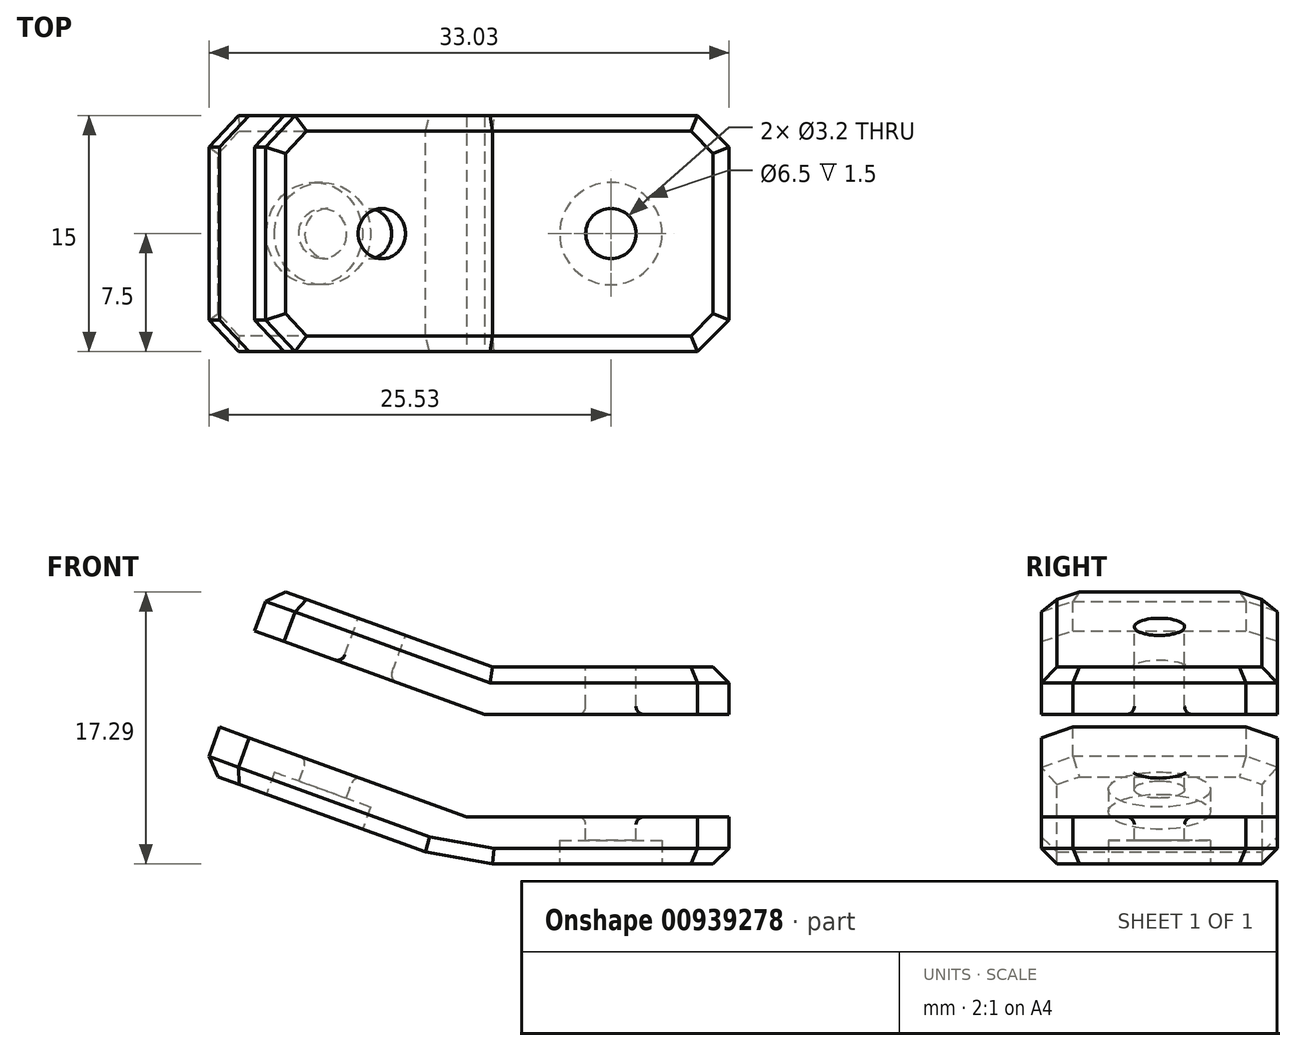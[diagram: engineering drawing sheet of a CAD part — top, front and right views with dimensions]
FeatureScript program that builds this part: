
annotation { "Feature Type Name" : "Feature", "Feature Type Description" : "" }
export const myFeature = defineFeature(function(context is Context, id is Id, definition is map)
    precondition{}
    {
        {
            var Q0;
            Q0=qCreatedBy(makeId("Front.planeOp"),FACE);
            var sketch = newSketch(context, id + "F0", { "sketchPlane" : qUnion([Q0])});
            skLineSegment(sketch, "E0", {"start": v(0, 0) * mm, "end": v(15, 0) * mm});
            skLineSegment(sketch, "E1", {"start": v(0, 0) * mm, "end": v(-14.1, 5.13) * mm});
            skLineSegment(sketch, "E2", {"start": v(-14.1, 5.13) * mm, "end": v(-15.12, 2.31) * mm});
            skLineSegment(sketch, "E3", {"start": v(-15.12, 2.31) * mm, "end": v(-1.03, -2.82) * mm});
            skLineSegment(sketch, "E4", {"start": v(-1.03, -2.82) * mm, "end": v(0, 0) * mm});
            skLineSegment(sketch, "E5", {"start": v(15, 0) * mm, "end": v(15, -3) * mm});
            skLineSegment(sketch, "E6", {"start": v(15, -3) * mm, "end": v(0, -3) * mm});
            skLineSegment(sketch, "E7", {"start": v(0, -3) * mm, "end": v(0, 0) * mm});
            skLineSegment(sketch, "E8", {"start": v(-15.12, 2.31) * mm, "end": v(-17.34, -3.8) * mm, "construction": true});
            skLineSegment(sketch, "E9", {"start": v(-17.34, -3.8) * mm, "end": v(-3.25, -8.93) * mm});
            skLineSegment(sketch, "E10", {"start": v(-3.25, -8.93) * mm, "end": v(-4.28, -11.75) * mm});
            skLineSegment(sketch, "E11", {"start": v(-4.28, -11.75) * mm, "end": v(-18.37, -6.62) * mm});
            skLineSegment(sketch, "E12", {"start": v(-18.37, -6.62) * mm, "end": v(-17.34, -3.8) * mm});
            skLineSegment(sketch, "E13", {"start": v(15, -3) * mm, "end": v(15, -9.5) * mm, "construction": true});
            skLineSegment(sketch, "E14", {"start": v(15, -9.5) * mm, "end": v(0, -9.5) * mm});
            skLineSegment(sketch, "E15", {"start": v(0, -9.5) * mm, "end": v(0, -12.5) * mm});
            skLineSegment(sketch, "E16", {"start": v(0, -12.5) * mm, "end": v(15, -12.5) * mm});
            skLineSegment(sketch, "E17", {"start": v(15, -12.5) * mm, "end": v(15, -9.5) * mm});
            skLineSegment(sketch, "E18", {"start": v(-4.28, -11.75) * mm, "end": v(0, -12.5) * mm});
            skLineSegment(sketch, "E19", {"start": v(-3.25, -8.93) * mm, "end": v(-1.03, -2.82) * mm});
            skLineSegment(sketch, "E20", {"start": v(0, -3) * mm, "end": v(0, -9.5) * mm});
            skSolve(sketch);
        }
        {
            var Q0;
            Q0 = qSketchRegion(id + "F0", true);
            extrude(context, id + "F1", {"entities" : qUnion([Q0]), "depth" : 15 * mm, "offsetDistance" : 25 * mm});
        }
        {
            var Q0;
            Q0=makeQuery(id+"F1.opExtrude","SWEPT_FACE",FACE,{"disambiguationData":[OSD([sQuery(id+"F0.wireOp",EDGE,"E1")])]});
            var sketch = newSketch(context, id + "F2", { "sketchPlane" : qUnion([Q0])});
            skLineSegment(sketch, "E21", {"start": v(-15, -7.5) * mm, "end": v(-7.5, -7.5) * mm, "construction": true});
            skPoint(sketch, "E21.endSnap0", {"position": v(-7.5, -15) * mm});
            skCircle(sketch, "E22", {"center": v(-7.5, -7.5) * mm, "radius": 1.6 * mm});
            skSolve(sketch);
        }
        {
            var Q0;
            Q0 = qSketchRegion(id + "F2", true);
            extrude(context, id + "F3", {"entities" : qUnion([Q0]), "operationType" : NewBodyOperationType.REMOVE, "oppositeDirection" : true, "depth" : 25 * mm, "offsetDistance" : 25 * mm});
        }
        {
            var Q0;
            Q0=makeQuery(id+"F1.opExtrude","SWEPT_FACE",FACE,{"disambiguationData":[OSD([sQuery(id+"F0.wireOp",EDGE,"E0")])]});
            var sketch = newSketch(context, id + "F4", { "sketchPlane" : qUnion([Q0])});
            skLineSegment(sketch, "E23", {"start": v(15, -7.5) * mm, "end": v(7.5, -7.5) * mm, "construction": true});
            skPoint(sketch, "E23.endSnap0", {"position": v(7.5, -15) * mm});
            skCircle(sketch, "E24", {"center": v(7.5, -7.5) * mm, "radius": 1.6 * mm});
            skSolve(sketch);
        }
        {
            var Q0;
            Q0 = qSketchRegion(id + "F4", true);
            extrude(context, id + "F5", {"entities" : qUnion([Q0]), "operationType" : NewBodyOperationType.REMOVE, "oppositeDirection" : true, "depth" : 25 * mm, "offsetDistance" : 25 * mm});
        }
        {
            var Q0;
            Q0=makeQuery(id+"F1.opExtrude","CAP_FACE",FACE,{"disambiguationData":[OSD([sQuery(id+"F0.wireOp",EDGE,"E0"),sQuery(id+"F0.wireOp",EDGE,"E1"),sQuery(id+"F0.wireOp",EDGE,"E2"),sQuery(id+"F0.wireOp",EDGE,"E3"),sQuery(id+"F0.wireOp",EDGE,"E5"),sQuery(id+"F0.wireOp",EDGE,"E6"),sQuery(id+"F0.wireOp",EDGE,"E9"),sQuery(id+"F0.wireOp",EDGE,"E11"),sQuery(id+"F0.wireOp",EDGE,"E12"),sQuery(id+"F0.wireOp",EDGE,"E14"),sQuery(id+"F0.wireOp",EDGE,"E16"),sQuery(id+"F0.wireOp",EDGE,"E17"),sQuery(id+"F0.wireOp",EDGE,"E18"),sQuery(id+"F0.wireOp",EDGE,"E19"),sQuery(id+"F0.wireOp",EDGE,"E20")])],"isStart":false});
            var sketch = newSketch(context, id + "F6", { "sketchPlane" : qUnion([Q0])});
            skLineSegment(sketch, "E25", {"start": v(0, 0) * mm, "end": v(-2.14, -12.12) * mm});
            skLineSegment(sketch, "E26", {"start": v(-15.12, 2.31) * mm, "end": v(-0.53, -3) * mm});
            skLineSegment(sketch, "E27", {"start": v(-0.53, -3) * mm, "end": v(15, -3) * mm});
            skLineSegment(sketch, "E28", {"start": v(-17.34, -3.8) * mm, "end": v(-1.68, -9.5) * mm});
            skLineSegment(sketch, "E29", {"start": v(-1.68, -9.5) * mm, "end": v(15, -9.5) * mm});
            skSolve(sketch);
        }
        {
            var Q0;
            {var subQ5=makeQuery(id+"F1.opExtrude","CAP_EDGE",EDGE,{"disambiguationData":[OSD([sQuery(id+"F0.wireOp",EDGE,"E19")])],"isStart":false});Q0=makeQuery(id+"F6.imprint","IMPRINT",FACE,{"disambiguationData":[TD([[makeQuery(id+"F6.imprint","IMPRINT",EDGE,{"derivedFrom":subQ5}),-1.0]])]});}
            var Q1;
            {var subQ5=makeQuery(id+"F1.opExtrude","CAP_EDGE",EDGE,{"disambiguationData":[OSD([sQuery(id+"F0.wireOp",EDGE,"E20")])],"isStart":false});Q1=makeQuery(id+"F6.imprint","IMPRINT",FACE,{"disambiguationData":[TD([[makeQuery(id+"F6.imprint","IMPRINT",EDGE,{"derivedFrom":subQ5}),-1.0]])]});}
            extrude(context, id + "F7", {"entities" : qUnion([Q0, Q1]), "operationType" : NewBodyOperationType.REMOVE, "oppositeDirection" : true, "depth" : 25 * mm, "offsetDistance" : 25 * mm});
        }
        {
            var Q0;
            Q0=makeQuery(id+"F1.opExtrude","SWEPT_FACE",FACE,{"disambiguationData":[OSD([sQuery(id+"F0.wireOp",EDGE,"E11")])]});
            var sketch = newSketch(context, id + "F8", { "sketchPlane" : qUnion([Q0])});
            skCircle(sketch, "E30", {"center": v(-7.5, 7.5) * mm, "radius": 3.25 * mm});
            skSolve(sketch);
        }
        {
            var Q0;
            Q0=makeQuery(id+"F8.imprint","IMPRINT",FACE,{"disambiguationData":[TD([[makeQuery(id+"F8.imprint","IMPRINT",EDGE,{"derivedFrom":sQuery(id+"F8.wireOp",EDGE,"E30")}),1.0]])]});
            extrude(context, id + "F9", {"entities" : qUnion([Q0]), "operationType" : NewBodyOperationType.REMOVE, "oppositeDirection" : true, "depth" : 1.5 * mm, "offsetDistance" : 25 * mm});
        }
        {
            var Q0;
            Q0=makeQuery(id+"F1.opExtrude","SWEPT_FACE",FACE,{"disambiguationData":[OSD([sQuery(id+"F0.wireOp",EDGE,"E16")])]});
            var sketch = newSketch(context, id + "F10", { "sketchPlane" : qUnion([Q0])});
            skCircle(sketch, "E31", {"center": v(7.5, 7.5) * mm, "radius": 3.25 * mm});
            skSolve(sketch);
        }
        {
            var Q0;
            Q0=makeQuery(id+"F10.imprint","IMPRINT",FACE,{"disambiguationData":[TD([[makeQuery(id+"F10.imprint","IMPRINT",EDGE,{"derivedFrom":sQuery(id+"F10.wireOp",EDGE,"E31")}),1.0]])]});
            extrude(context, id + "F11", {"entities" : qUnion([Q0]), "operationType" : NewBodyOperationType.REMOVE, "oppositeDirection" : true, "depth" : 1.5 * mm, "offsetDistance" : 25 * mm});
        }
        {
            var Q0;
            Q0=makeQuery(id+"F1.opExtrude","CAP_EDGE",EDGE,{"disambiguationData":[OSD([sQuery(id+"F0.wireOp",EDGE,"E2")])],"isStart":false});
            var Q1;
            Q1=makeQuery(id+"F1.opExtrude","CAP_EDGE",EDGE,{"disambiguationData":[OSD([sQuery(id+"F0.wireOp",EDGE,"E12")])],"isStart":false});
            var Q2;
            Q2=makeQuery(id+"F1.opExtrude","CAP_EDGE",EDGE,{"disambiguationData":[OSD([sQuery(id+"F0.wireOp",EDGE,"E2")])],"isStart":true});
            var Q3;
            Q3=makeQuery(id+"F1.opExtrude","CAP_EDGE",EDGE,{"disambiguationData":[OSD([sQuery(id+"F0.wireOp",EDGE,"E12")])],"isStart":true});
            var Q4;
            Q4=makeQuery(id+"F1.opExtrude","CAP_EDGE",EDGE,{"disambiguationData":[OSD([sQuery(id+"F0.wireOp",EDGE,"E17")])],"isStart":false});
            var Q5;
            Q5=makeQuery(id+"F1.opExtrude","CAP_EDGE",EDGE,{"disambiguationData":[OSD([sQuery(id+"F0.wireOp",EDGE,"E17")])],"isStart":true});
            var Q6;
            Q6=makeQuery(id+"F1.opExtrude","CAP_EDGE",EDGE,{"disambiguationData":[OSD([sQuery(id+"F0.wireOp",EDGE,"E5")])],"isStart":true});
            var Q7;
            Q7=makeQuery(id+"F1.opExtrude","CAP_EDGE",EDGE,{"disambiguationData":[OSD([sQuery(id+"F0.wireOp",EDGE,"E5")])],"isStart":false});
            chamfer(context, id + "F12", {"entities" : qUnion([Q0, Q1, Q2, Q3, Q4, Q5, Q6, Q7]), "width" : 2 * mm, "tangentPropagation" : true});
        }
        {
            var Q0;
            Q0=makeQuery(id+"F1.opExtrude","SWEPT_EDGE",EDGE,{"disambiguationData":[OSD([sQuery(id+"F0.wireOp",EDGE,"E11"),sQuery(id+"F0.wireOp",EDGE,"E12")])]});
            var Q1;
            Q1=makeQuery(id+"F12.opChamfer","BLEND_EDGE",EDGE,{"blendedFrom":[makeQuery(id+"F1.opExtrude","CAP_EDGE",EDGE,{"disambiguationData":[OSD([sQuery(id+"F0.wireOp",EDGE,"E12")])],"isStart":false}),makeQuery(id+"F1.opExtrude","SWEPT_FACE",FACE,{"disambiguationData":[OSD([sQuery(id+"F0.wireOp",EDGE,"E11")])]})],"blendedInto":[makeQuery(id+"F1.opExtrude","SWEPT_FACE",FACE,{"disambiguationData":[OSD([sQuery(id+"F0.wireOp",EDGE,"E11")])]})]});
            var Q2;
            Q2=makeQuery(id+"F1.opExtrude","CAP_EDGE",EDGE,{"disambiguationData":[OSD([sQuery(id+"F0.wireOp",EDGE,"E11")])],"isStart":false});
            var Q3;
            Q3=makeQuery(id+"F12.opChamfer","BLEND_EDGE",EDGE,{"blendedFrom":[makeQuery(id+"F1.opExtrude","CAP_EDGE",EDGE,{"disambiguationData":[OSD([sQuery(id+"F0.wireOp",EDGE,"E12")])],"isStart":true}),makeQuery(id+"F1.opExtrude","SWEPT_FACE",FACE,{"disambiguationData":[OSD([sQuery(id+"F0.wireOp",EDGE,"E11")])]})],"blendedInto":[makeQuery(id+"F1.opExtrude","SWEPT_FACE",FACE,{"disambiguationData":[OSD([sQuery(id+"F0.wireOp",EDGE,"E11")])]})]});
            var Q4;
            Q4=makeQuery(id+"F1.opExtrude","CAP_EDGE",EDGE,{"disambiguationData":[OSD([sQuery(id+"F0.wireOp",EDGE,"E11")])],"isStart":true});
            var Q5;
            Q5=makeQuery(id+"F1.opExtrude","CAP_EDGE",EDGE,{"disambiguationData":[OSD([sQuery(id+"F0.wireOp",EDGE,"E18")])],"isStart":true});
            var Q6;
            Q6=makeQuery(id+"F1.opExtrude","CAP_EDGE",EDGE,{"disambiguationData":[OSD([sQuery(id+"F0.wireOp",EDGE,"E18")])],"isStart":false});
            var Q7;
            Q7=makeQuery(id+"F1.opExtrude","CAP_EDGE",EDGE,{"disambiguationData":[OSD([sQuery(id+"F0.wireOp",EDGE,"E16")])],"isStart":false});
            var Q8;
            Q8=makeQuery(id+"F1.opExtrude","CAP_EDGE",EDGE,{"disambiguationData":[OSD([sQuery(id+"F0.wireOp",EDGE,"E16")])],"isStart":true});
            var Q9;
            Q9=makeQuery(id+"F12.opChamfer","BLEND_EDGE",EDGE,{"blendedFrom":[makeQuery(id+"F1.opExtrude","CAP_EDGE",EDGE,{"disambiguationData":[OSD([sQuery(id+"F0.wireOp",EDGE,"E17")])],"isStart":true}),makeQuery(id+"F1.opExtrude","SWEPT_FACE",FACE,{"disambiguationData":[OSD([sQuery(id+"F0.wireOp",EDGE,"E16")])]})],"blendedInto":[makeQuery(id+"F1.opExtrude","SWEPT_FACE",FACE,{"disambiguationData":[OSD([sQuery(id+"F0.wireOp",EDGE,"E16")])]})]});
            var Q10;
            Q10=makeQuery(id+"F1.opExtrude","SWEPT_EDGE",EDGE,{"disambiguationData":[OSD([sQuery(id+"F0.wireOp",EDGE,"E16"),sQuery(id+"F0.wireOp",EDGE,"E17")])]});
            var Q11;
            Q11=makeQuery(id+"F12.opChamfer","BLEND_EDGE",EDGE,{"blendedFrom":[makeQuery(id+"F1.opExtrude","CAP_EDGE",EDGE,{"disambiguationData":[OSD([sQuery(id+"F0.wireOp",EDGE,"E17")])],"isStart":false}),makeQuery(id+"F1.opExtrude","SWEPT_FACE",FACE,{"disambiguationData":[OSD([sQuery(id+"F0.wireOp",EDGE,"E16")])]})],"blendedInto":[makeQuery(id+"F1.opExtrude","SWEPT_FACE",FACE,{"disambiguationData":[OSD([sQuery(id+"F0.wireOp",EDGE,"E16")])]})]});
            chamfer(context, id + "F13", {"entities" : qUnion([Q0, Q1, Q2, Q3, Q4, Q5, Q6, Q7, Q8, Q9, Q10, Q11]), "width" : 1 * mm, "tangentPropagation" : true});
        }
        {
            var Q0;
            Q0=makeQuery(id+"F9.boolean.opBoolean","COPY",EDGE,{"derivedFrom":makeQuery(id+"F9.opExtrude","CAP_EDGE",EDGE,{"disambiguationData":[OSD([sQuery(id+"F0.wireOp",EDGE,"E11"),sQuery(id+"F2.wireOp",EDGE,"E22")])],"isStart":false})});
            var Q1;
            Q1=makeQuery(id+"F11.boolean.opBoolean","COPY",EDGE,{"derivedFrom":makeQuery(id+"F11.opExtrude","CAP_EDGE",EDGE,{"disambiguationData":[OSD([sQuery(id+"F0.wireOp",EDGE,"E16"),sQuery(id+"F4.wireOp",EDGE,"E24")])],"isStart":false})});
            var Q2;
            Q2=makeQuery(id+"F5.boolean.opBoolean","INTERSECT",EDGE,{"derivedFrom":[makeQuery(id+"F1.opExtrude","SWEPT_FACE",FACE,{"disambiguationData":[OSD([sQuery(id+"F0.wireOp",EDGE,"E14")])]}),makeQuery(id+"F5.opExtrude","SWEPT_FACE",FACE,{"disambiguationData":[OSD([sQuery(id+"F4.wireOp",EDGE,"E24")])]})]});
            var Q3;
            Q3=makeQuery(id+"F3.boolean.opBoolean","INTERSECT",EDGE,{"derivedFrom":[makeQuery(id+"F1.opExtrude","SWEPT_FACE",FACE,{"disambiguationData":[OSD([sQuery(id+"F0.wireOp",EDGE,"E9")])]}),makeQuery(id+"F3.opExtrude","SWEPT_FACE",FACE,{"disambiguationData":[OSD([sQuery(id+"F2.wireOp",EDGE,"E22")])]})]});
            var Q4;
            Q4=makeQuery(id+"F3.boolean.opBoolean","COPY",EDGE,{"derivedFrom":makeQuery(id+"F3.opExtrude","CAP_EDGE",EDGE,{"disambiguationData":[OSD([sQuery(id+"F2.wireOp",EDGE,"E22")])],"isStart":true})});
            var Q5;
            Q5=makeQuery(id+"F5.boolean.opBoolean","COPY",EDGE,{"derivedFrom":makeQuery(id+"F5.opExtrude","CAP_EDGE",EDGE,{"disambiguationData":[OSD([sQuery(id+"F4.wireOp",EDGE,"E24")])],"isStart":true})});
            var Q6;
            Q6=makeQuery(id+"F3.boolean.opBoolean","INTERSECT",EDGE,{"derivedFrom":[makeQuery(id+"F1.opExtrude","SWEPT_FACE",FACE,{"disambiguationData":[OSD([sQuery(id+"F0.wireOp",EDGE,"E3")])]}),makeQuery(id+"F3.opExtrude","SWEPT_FACE",FACE,{"disambiguationData":[OSD([sQuery(id+"F2.wireOp",EDGE,"E22")])]})]});
            var Q7;
            Q7=makeQuery(id+"F5.boolean.opBoolean","INTERSECT",EDGE,{"derivedFrom":[makeQuery(id+"F1.opExtrude","SWEPT_FACE",FACE,{"disambiguationData":[OSD([sQuery(id+"F0.wireOp",EDGE,"E6")])]}),makeQuery(id+"F5.opExtrude","SWEPT_FACE",FACE,{"disambiguationData":[OSD([sQuery(id+"F4.wireOp",EDGE,"E24")])]})]});
            fillet(context, id + "F14", {"entities" : qUnion([Q0, Q1, Q2, Q3, Q4, Q5, Q6, Q7]), "radius" : .5 * mm, "tangentPropagation" : true, "allowEdgeOverflow" : false});
        }
        {
            var Q0;
            Q0=makeQuery(id+"F1.opExtrude","CAP_EDGE",EDGE,{"disambiguationData":[OSD([sQuery(id+"F0.wireOp",EDGE,"E1")])],"isStart":false});
            var Q1;
            Q1=makeQuery(id+"F1.opExtrude","CAP_EDGE",EDGE,{"disambiguationData":[OSD([sQuery(id+"F0.wireOp",EDGE,"E0")])],"isStart":false});
            var Q2;
            Q2=makeQuery(id+"F12.opChamfer","BLEND_EDGE",EDGE,{"blendedFrom":[makeQuery(id+"F1.opExtrude","CAP_EDGE",EDGE,{"disambiguationData":[OSD([sQuery(id+"F0.wireOp",EDGE,"E5")])],"isStart":false}),makeQuery(id+"F1.opExtrude","SWEPT_FACE",FACE,{"disambiguationData":[OSD([sQuery(id+"F0.wireOp",EDGE,"E0")])]})],"blendedInto":[makeQuery(id+"F1.opExtrude","SWEPT_FACE",FACE,{"disambiguationData":[OSD([sQuery(id+"F0.wireOp",EDGE,"E0")])]})]});
            var Q3;
            Q3=makeQuery(id+"F1.opExtrude","SWEPT_EDGE",EDGE,{"disambiguationData":[OSD([sQuery(id+"F0.wireOp",EDGE,"E0"),sQuery(id+"F0.wireOp",EDGE,"E5")])]});
            var Q4;
            Q4=makeQuery(id+"F12.opChamfer","BLEND_EDGE",EDGE,{"blendedFrom":[makeQuery(id+"F1.opExtrude","CAP_EDGE",EDGE,{"disambiguationData":[OSD([sQuery(id+"F0.wireOp",EDGE,"E5")])],"isStart":true}),makeQuery(id+"F1.opExtrude","SWEPT_FACE",FACE,{"disambiguationData":[OSD([sQuery(id+"F0.wireOp",EDGE,"E0")])]})],"blendedInto":[makeQuery(id+"F1.opExtrude","SWEPT_FACE",FACE,{"disambiguationData":[OSD([sQuery(id+"F0.wireOp",EDGE,"E0")])]})]});
            var Q5;
            Q5=makeQuery(id+"F1.opExtrude","CAP_EDGE",EDGE,{"disambiguationData":[OSD([sQuery(id+"F0.wireOp",EDGE,"E0")])],"isStart":true});
            var Q6;
            Q6=makeQuery(id+"F1.opExtrude","CAP_EDGE",EDGE,{"disambiguationData":[OSD([sQuery(id+"F0.wireOp",EDGE,"E1")])],"isStart":true});
            var Q7;
            Q7=makeQuery(id+"F12.opChamfer","BLEND_EDGE",EDGE,{"blendedFrom":[makeQuery(id+"F1.opExtrude","CAP_EDGE",EDGE,{"disambiguationData":[OSD([sQuery(id+"F0.wireOp",EDGE,"E2")])],"isStart":false}),makeQuery(id+"F1.opExtrude","SWEPT_FACE",FACE,{"disambiguationData":[OSD([sQuery(id+"F0.wireOp",EDGE,"E1")])]})],"blendedInto":[makeQuery(id+"F1.opExtrude","SWEPT_FACE",FACE,{"disambiguationData":[OSD([sQuery(id+"F0.wireOp",EDGE,"E1")])]})]});
            var Q8;
            Q8=makeQuery(id+"F1.opExtrude","SWEPT_EDGE",EDGE,{"disambiguationData":[OSD([sQuery(id+"F0.wireOp",EDGE,"E1"),sQuery(id+"F0.wireOp",EDGE,"E2")])]});
            var Q9;
            Q9=makeQuery(id+"F12.opChamfer","BLEND_EDGE",EDGE,{"blendedFrom":[makeQuery(id+"F1.opExtrude","CAP_EDGE",EDGE,{"disambiguationData":[OSD([sQuery(id+"F0.wireOp",EDGE,"E2")])],"isStart":true}),makeQuery(id+"F1.opExtrude","SWEPT_FACE",FACE,{"disambiguationData":[OSD([sQuery(id+"F0.wireOp",EDGE,"E1")])]})],"blendedInto":[makeQuery(id+"F1.opExtrude","SWEPT_FACE",FACE,{"disambiguationData":[OSD([sQuery(id+"F0.wireOp",EDGE,"E1")])]})]});
            chamfer(context, id + "F15", {"entities" : qUnion([Q0, Q1, Q2, Q3, Q4, Q5, Q6, Q7, Q8, Q9]), "width" : 1 * mm, "tangentPropagation" : true});
        }
    });
